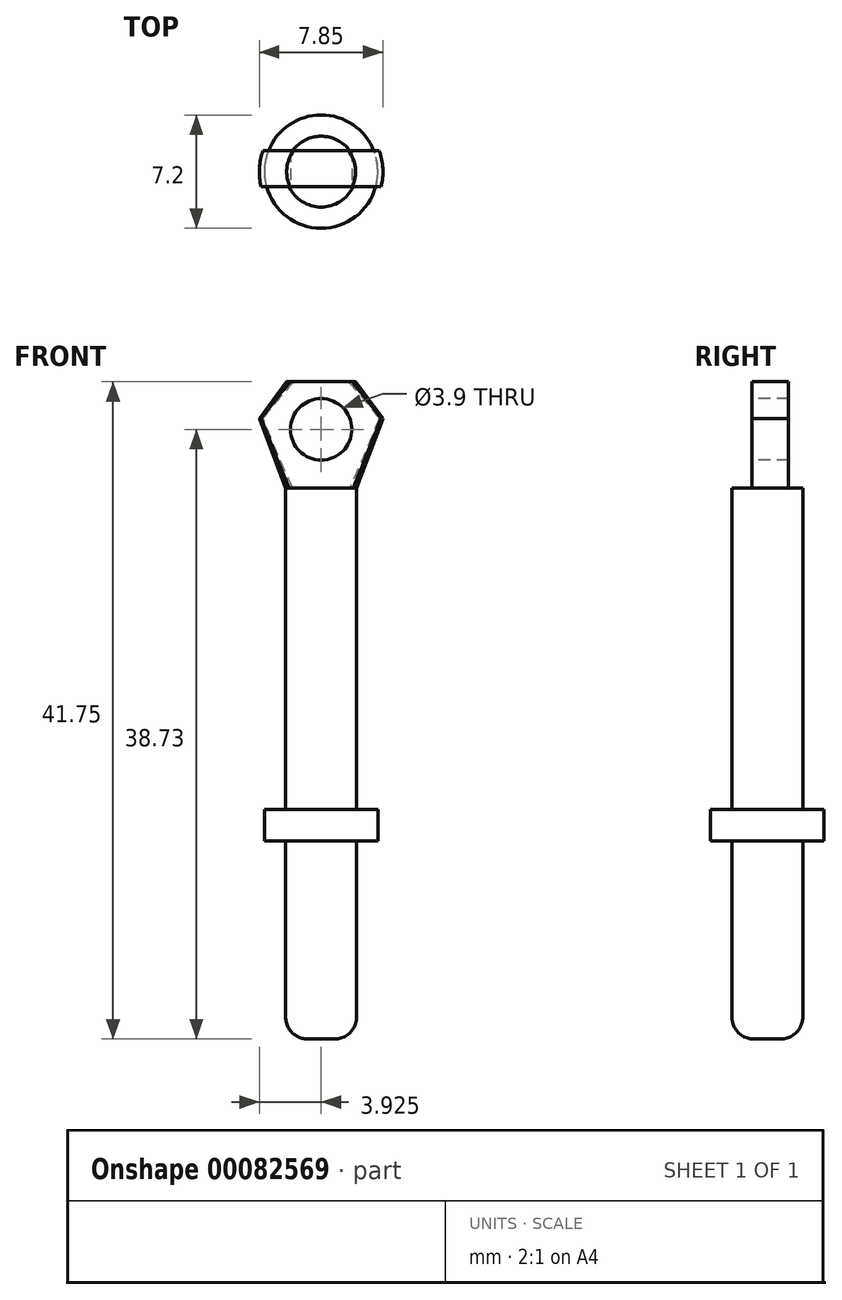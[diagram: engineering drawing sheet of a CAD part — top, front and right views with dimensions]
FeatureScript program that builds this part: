
annotation { "Feature Type Name" : "Feature", "Feature Type Description" : "" }
export const myFeature = defineFeature(function(context is Context, id is Id, definition is map)
    precondition{}
    {
        {
            var Q0;
            Q0=qCreatedBy(makeId("Front.planeOp"),FACE);
            var sketch = newSketch(context, id + "F0", { "sketchPlane" : qUnion([Q0])});
            skLineSegment(sketch, "E0", {"start": v(-3.07, -26.94) * mm, "end": v(-3.07, 17.84) * mm, "construction": true});
            skLineSegment(sketch, "E1", {"start": v(-5.32, 8.06) * mm, "end": v(-5.32, -12.34) * mm});
            skLineSegment(sketch, "E2", {"start": v(-5.32, -12.34) * mm, "end": v(-6.67, -12.34) * mm});
            skLineSegment(sketch, "E3", {"start": v(-6.67, -12.34) * mm, "end": v(-6.67, -14.34) * mm});
            skLineSegment(sketch, "E4", {"start": v(-6.67, -14.34) * mm, "end": v(-5.32, -14.34) * mm});
            skLineSegment(sketch, "E5", {"start": v(-5.32, -14.34) * mm, "end": v(-5.32, -25.54) * mm});
            skLineSegment(sketch, "E6", {"start": v(-3.92, -26.94) * mm, "end": v(-3.07, -26.94) * mm});
            skLineSegment(sketch, "E7", {"start": v(-5.32, 8.06) * mm, "end": v(-7, 12.49) * mm});
            skLineSegment(sketch, "E8", {"start": v(-7, 12.49) * mm, "end": v(-5.26, 14.81) * mm});
            skLineSegment(sketch, "E9", {"start": v(-5.26, 14.81) * mm, "end": v(-3.07, 14.81) * mm});
            skLineSegment(sketch, "E10", {"start": v(-3.07, 14.81) * mm, "end": v(-3.07, 13.3) * mm});
            skArc(sketch, "E11", {"start": v(-3.07, 10.27) * mm, "mid": v(-4.59, 11.79) * mm, "end": v(-3.07, 13.3) * mm});
            skPoint(sketch, "E11.startSnap0", {"position": v(-6.16, 10.27) * mm});
            skLineSegment(sketch, "E12.trimOffspring", {"start": v(-3.07, 10.27) * mm, "end": v(-3.07, -26.94) * mm});
            skPoint(sketch, "E13.visualSharp", {"position": v(-5.32, -26.94) * mm});
            skArc(sketch, "E13.filletArc", {"start": v(-5.32, -25.54) * mm, "mid": v(-4.91, -26.53) * mm, "end": v(-3.92, -26.94) * mm});
            skLineSegment(sketch, "E14", {"start": v(-5.32, -19.94) * mm, "end": v(0.97, -19.94) * mm, "construction": true});
            skSolve(sketch);
        }
        {
            var Q0;
            Q0 = qSketchRegion(id + "F0", true);
            var Q1;
            Q1=sQuery(id+"F0.wireOp",EDGE,"E0");
            revolve(context, id + "F1", {"entities" : qUnion([Q0]), "axis" : qUnion([Q1]), "revolveType" : RevolveType.FULL});
        }
        {
            var Q0;
            Q0=qCreatedBy(makeId("Front.planeOp"),FACE);
            var sketch = newSketch(context, id + "F2", { "sketchPlane" : qUnion([Q0])});
            skLineSegment(sketch, "E15.bottom", {"start": v(-8.54, 15.52) * mm, "end": v(3.14, 15.52) * mm});
            skLineSegment(sketch, "E15.top", {"start": v(-8.54, 8.06) * mm, "end": v(3.14, 8.06) * mm});
            skLineSegment(sketch, "E15.left", {"start": v(-8.54, 15.52) * mm, "end": v(-8.54, 8.06) * mm});
            skLineSegment(sketch, "E15.right", {"start": v(3.14, 15.52) * mm, "end": v(3.14, 8.06) * mm});
            skSolve(sketch);
        }
        {
            var Q0;
            Q0 = qSketchRegion(id + "F2", true);
            extrude(context, id + "F3", {"entities" : qUnion([Q0]), "operationType" : NewBodyOperationType.REMOVE, "oppositeDirection" : true, "depth" : 25 * mm, "hasSecondDirection" : true, "secondDirectionOppositeDirection" : true, "secondDirectionDepth" : 1.35 * mm});
        }
        {
            var Q0;
            Q0=qCreatedBy(makeId("Front.planeOp"),FACE);
            var sketch = newSketch(context, id + "F4", { "sketchPlane" : qUnion([Q0])});
            skLineSegment(sketch, "E16.bottom", {"start": v(-8.9, 15.24) * mm, "end": v(1.9, 15.24) * mm});
            skLineSegment(sketch, "E16.top", {"start": v(-8.9, 8.06) * mm, "end": v(1.9, 8.06) * mm});
            skLineSegment(sketch, "E16.left", {"start": v(-8.9, 15.24) * mm, "end": v(-8.9, 8.06) * mm});
            skLineSegment(sketch, "E16.right", {"start": v(1.9, 15.24) * mm, "end": v(1.9, 8.06) * mm});
            skSolve(sketch);
        }
        {
            var Q0;
            Q0 = qSketchRegion(id + "F4", true);
            extrude(context, id + "F5", {"entities" : qUnion([Q0]), "operationType" : NewBodyOperationType.REMOVE, "depth" : 8.07 * mm, "hasSecondDirection" : true, "secondDirectionOppositeDirection" : false, "secondDirectionDepth" : 0.97 * mm});
        }
        {
            var Q0;
            Q0=makeQuery(id+"F5.boolean.opBoolean","COPY",FACE,{"derivedFrom":makeQuery(id+"F5.opExtrude","CAP_FACE",FACE,{"disambiguationData":[OSD([sQuery(id+"F4.wireOp",EDGE,"E16.bottom"),sQuery(id+"F4.wireOp",EDGE,"E16.top"),sQuery(id+"F4.wireOp",EDGE,"E16.left"),sQuery(id+"F4.wireOp",EDGE,"E16.right")])],"isStart":true})});
            var sketch = newSketch(context, id + "F6", { "sketchPlane" : qUnion([Q0])});
            skCircle(sketch, "E17", {"center": v(-3.07, 11.79) * mm, "radius": 1.95 * mm});
            skSolve(sketch);
        }
        {
            var Q0;
            Q0 = qSketchRegion(id + "F6", true);
            extrude(context, id + "F7", {"entities" : qUnion([Q0]), "operationType" : NewBodyOperationType.REMOVE, "endBound" : BoundingType.SYMMETRIC, "oppositeDirection" : true, "depth" : 25 * mm});
        }
    });
